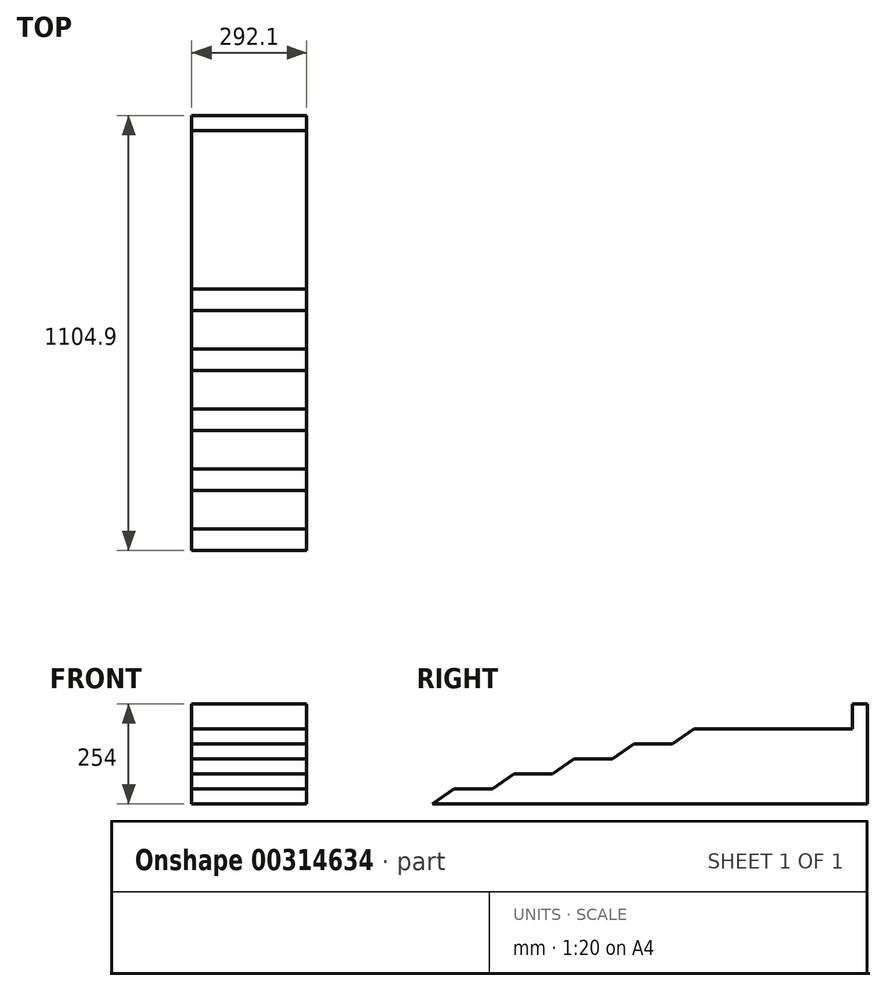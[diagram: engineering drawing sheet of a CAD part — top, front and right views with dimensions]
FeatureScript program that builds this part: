
annotation { "Feature Type Name" : "Feature", "Feature Type Description" : "" }
export const myFeature = defineFeature(function(context is Context, id is Id, definition is map)
    precondition{}
    {
        {
            var Q0;
            Q0=qCreatedBy(makeId("Right.planeOp"),FACE);
            var sketch = newSketch(context, id + "F0", { "sketchPlane" : qUnion([Q0])});
            skLineSegment(sketch, "E0.bottom", {"start": v(0, 0) * mm, "end": v(1066.8, 0) * mm});
            skLineSegment(sketch, "E0.top", {"start": v(0, 38.1) * mm, "end": v(1066.8, 38.1) * mm});
            skLineSegment(sketch, "E0.left", {"start": v(0, 0) * mm, "end": v(0, 38.1) * mm});
            skLineSegment(sketch, "E0.right", {"start": v(1066.8, 0) * mm, "end": v(1066.8, 38.1) * mm});
            skSolve(sketch);
        }
        {
            var Q0;
            Q0 = qSketchRegion(id + "F0", true);
            extrude(context, id + "F1", {"entities" : qUnion([Q0]), "depth" : 292.1 * mm});
        }
        {
            var Q0;
            Q0=qCreatedBy(makeId("Right.planeOp"),FACE);
            var sketch = newSketch(context, id + "F2", { "sketchPlane" : qUnion([Q0])});
            skLineSegment(sketch, "E1.bottom", {"start": v(1066.8, 38.1) * mm, "end": v(152.4, 38.1) * mm});
            skLineSegment(sketch, "E1.top", {"start": v(1066.8, 76.2) * mm, "end": v(152.4, 76.2) * mm});
            skLineSegment(sketch, "E1.left", {"start": v(1066.8, 38.1) * mm, "end": v(1066.8, 76.2) * mm});
            skLineSegment(sketch, "E1.right", {"start": v(152.4, 38.1) * mm, "end": v(152.4, 76.2) * mm});
            skSolve(sketch);
        }
        {
            var Q0;
            Q0 = qSketchRegion(id + "F2", true);
            var Q1;
            Q1=makeQuery(id+"F1.opExtrude","CAP_FACE",FACE,{"disambiguationData":[OSD([sQuery(id+"F0.wireOp",EDGE,"E0.bottom"),sQuery(id+"F0.wireOp",EDGE,"E0.top"),sQuery(id+"F0.wireOp",EDGE,"E0.left"),sQuery(id+"F0.wireOp",EDGE,"E0.right")])],"isStart":false});
            extrude(context, id + "F3", {"entities" : qUnion([Q0]), "operationType" : NewBodyOperationType.ADD, "endBound" : BoundingType.UP_TO_SURFACE, "endBoundEntityFace" : qUnion([Q1]), "depth" : 25.4 * mm});
        }
        {
            var Q0;
            Q0=qCreatedBy(makeId("Right.planeOp"),FACE);
            var sketch = newSketch(context, id + "F4", { "sketchPlane" : qUnion([Q0])});
            skLineSegment(sketch, "E2.bottom", {"start": v(1066.8, 76.2) * mm, "end": v(304.8, 76.2) * mm});
            skLineSegment(sketch, "E2.top", {"start": v(1066.8, 114.3) * mm, "end": v(304.8, 114.3) * mm});
            skLineSegment(sketch, "E2.left", {"start": v(1066.8, 76.2) * mm, "end": v(1066.8, 114.3) * mm});
            skLineSegment(sketch, "E2.right", {"start": v(304.8, 76.2) * mm, "end": v(304.8, 114.3) * mm});
            skSolve(sketch);
        }
        {
            var Q0;
            Q0 = qSketchRegion(id + "F4", true);
            var Q1;
            {var subQ0=sQuery(id+"F0.wireOp",EDGE,"E0.right");var subQ1=sQuery(id+"F0.wireOp",EDGE,"E0.left");var subQ2=sQuery(id+"F0.wireOp",EDGE,"E0.top");var subQ3=sQuery(id+"F0.wireOp",EDGE,"E0.bottom");Q1=makeQuery(id+"F3.boolean.opBoolean","MERGE",FACE,{"derivedFrom":[makeQuery(id+"F1.opExtrude","CAP_FACE",FACE,{"disambiguationData":[OSD([subQ3,subQ2,subQ1,subQ0])],"isStart":false}),makeQuery(id+"F3.opExtrude","CAP_FACE",FACE,{"disambiguationData":[OSD([subQ3,subQ2,subQ1,subQ0])],"isStart":false})]});}
            extrude(context, id + "F5", {"entities" : qUnion([Q0]), "operationType" : NewBodyOperationType.ADD, "endBound" : BoundingType.UP_TO_SURFACE, "endBoundEntityFace" : qUnion([Q1]), "depth" : 25.4 * mm});
        }
        {
            var Q0;
            Q0=qCreatedBy(makeId("Right.planeOp"),FACE);
            var sketch = newSketch(context, id + "F6", { "sketchPlane" : qUnion([Q0])});
            skLineSegment(sketch, "E3.bottom", {"start": v(457.2, 152.4) * mm, "end": v(1066.8, 152.4) * mm});
            skLineSegment(sketch, "E3.top", {"start": v(457.2, 114.3) * mm, "end": v(1066.8, 114.3) * mm});
            skLineSegment(sketch, "E3.left", {"start": v(457.2, 152.4) * mm, "end": v(457.2, 114.3) * mm});
            skLineSegment(sketch, "E3.right", {"start": v(1066.8, 152.4) * mm, "end": v(1066.8, 114.3) * mm});
            skSolve(sketch);
        }
        {
            var Q0;
            Q0 = qSketchRegion(id + "F6", true);
            var Q1;
            {var subQ0=sQuery(id+"F0.wireOp",EDGE,"E0.right");var subQ1=sQuery(id+"F0.wireOp",EDGE,"E0.left");var subQ2=sQuery(id+"F0.wireOp",EDGE,"E0.top");var subQ3=sQuery(id+"F0.wireOp",EDGE,"E0.bottom");Q1=makeQuery(id+"F5.boolean.opBoolean","MERGE",FACE,{"derivedFrom":[makeQuery(id+"F3.boolean.opBoolean","MERGE",FACE,{"derivedFrom":[makeQuery(id+"F1.opExtrude","CAP_FACE",FACE,{"disambiguationData":[OSD([subQ3,subQ2,subQ1,subQ0])],"isStart":false}),makeQuery(id+"F3.opExtrude","CAP_FACE",FACE,{"disambiguationData":[OSD([subQ3,subQ2,subQ1,subQ0])],"isStart":false})]}),makeQuery(id+"F5.opExtrude","CAP_FACE",FACE,{"disambiguationData":[OSD([subQ3,subQ2,subQ1,subQ0])],"isStart":false})]});}
            extrude(context, id + "F7", {"entities" : qUnion([Q0]), "operationType" : NewBodyOperationType.ADD, "endBound" : BoundingType.UP_TO_SURFACE, "endBoundEntityFace" : qUnion([Q1]), "depth" : 25.4 * mm});
        }
        {
            var Q0;
            Q0=qCreatedBy(makeId("Right.planeOp"),FACE);
            var sketch = newSketch(context, id + "F8", { "sketchPlane" : qUnion([Q0])});
            skLineSegment(sketch, "E4.bottom", {"start": v(609.6, 190.5) * mm, "end": v(1066.8, 190.5) * mm});
            skLineSegment(sketch, "E4.top", {"start": v(609.6, 152.4) * mm, "end": v(1066.8, 152.4) * mm});
            skLineSegment(sketch, "E4.left", {"start": v(609.6, 190.5) * mm, "end": v(609.6, 152.4) * mm});
            skLineSegment(sketch, "E4.right", {"start": v(1066.8, 190.5) * mm, "end": v(1066.8, 152.4) * mm});
            skSolve(sketch);
        }
        {
            var Q0;
            Q0 = qSketchRegion(id + "F8", true);
            var Q1;
            {var subQ0=sQuery(id+"F0.wireOp",EDGE,"E0.right");var subQ1=sQuery(id+"F0.wireOp",EDGE,"E0.left");var subQ2=sQuery(id+"F0.wireOp",EDGE,"E0.top");var subQ3=sQuery(id+"F0.wireOp",EDGE,"E0.bottom");Q1=makeQuery(id+"F7.boolean.opBoolean","MERGE",FACE,{"derivedFrom":[makeQuery(id+"F5.boolean.opBoolean","MERGE",FACE,{"derivedFrom":[makeQuery(id+"F3.boolean.opBoolean","MERGE",FACE,{"derivedFrom":[makeQuery(id+"F1.opExtrude","CAP_FACE",FACE,{"disambiguationData":[OSD([subQ3,subQ2,subQ1,subQ0])],"isStart":false}),makeQuery(id+"F3.opExtrude","CAP_FACE",FACE,{"disambiguationData":[OSD([subQ3,subQ2,subQ1,subQ0])],"isStart":false})]}),makeQuery(id+"F5.opExtrude","CAP_FACE",FACE,{"disambiguationData":[OSD([subQ3,subQ2,subQ1,subQ0])],"isStart":false})]}),makeQuery(id+"F7.opExtrude","CAP_FACE",FACE,{"disambiguationData":[OSD([subQ3,subQ2,subQ1,subQ0])],"isStart":false})]});}
            extrude(context, id + "F9", {"entities" : qUnion([Q0]), "operationType" : NewBodyOperationType.ADD, "endBound" : BoundingType.UP_TO_SURFACE, "endBoundEntityFace" : qUnion([Q1]), "depth" : 25.4 * mm});
        }
        {
            var Q0;
            Q0=makeQuery(id+"F1.opExtrude","SWEPT_EDGE",EDGE,{"disambiguationData":[OSD([sQuery(id+"F0.wireOp",EDGE,"E0.top"),sQuery(id+"F0.wireOp",EDGE,"E0.left")])]});
            var Q1;
            Q1=makeQuery(id+"F3.opExtrude","SWEPT_EDGE",EDGE,{"disambiguationData":[OSD([sQuery(id+"F2.wireOp",EDGE,"E1.top"),sQuery(id+"F2.wireOp",EDGE,"E1.right")])]});
            var Q2;
            Q2=makeQuery(id+"F5.opExtrude","SWEPT_EDGE",EDGE,{"disambiguationData":[OSD([sQuery(id+"F4.wireOp",EDGE,"E2.top"),sQuery(id+"F4.wireOp",EDGE,"E2.right")])]});
            var Q3;
            Q3=makeQuery(id+"F7.opExtrude","SWEPT_EDGE",EDGE,{"disambiguationData":[OSD([sQuery(id+"F6.wireOp",EDGE,"E3.bottom"),sQuery(id+"F6.wireOp",EDGE,"E3.left")])]});
            var Q4;
            Q4=makeQuery(id+"F9.opExtrude","SWEPT_EDGE",EDGE,{"disambiguationData":[OSD([sQuery(id+"F8.wireOp",EDGE,"E4.bottom"),sQuery(id+"F8.wireOp",EDGE,"E4.left")])]});
            chamfer(context, id + "F10", {"entities" : qUnion([Q0, Q1, Q2, Q3, Q4]), "chamferType" : ChamferType.OFFSET_ANGLE, "width" : 38.1 * mm, "oppositeDirection" : false, "angle" : 55 * degree, "tangentPropagation" : true});
        }
        {
            var Q0;
            Q0=qCreatedBy(makeId("Top.planeOp"),FACE);
            var sketch = newSketch(context, id + "F11", { "sketchPlane" : qUnion([Q0])});
            skLineSegment(sketch, "E5.bottom", {"start": v(0, 1066.8) * mm, "end": v(292.1, 1066.8) * mm});
            skLineSegment(sketch, "E5.top", {"start": v(0, 1104.9) * mm, "end": v(292.1, 1104.9) * mm});
            skLineSegment(sketch, "E5.left", {"start": v(0, 1066.8) * mm, "end": v(0, 1104.9) * mm});
            skLineSegment(sketch, "E5.right", {"start": v(292.1, 1066.8) * mm, "end": v(292.1, 1104.9) * mm});
            skSolve(sketch);
        }
        {
            var Q0;
            Q0 = qSketchRegion(id + "F11", true);
            extrude(context, id + "F12", {"entities" : qUnion([Q0]), "operationType" : NewBodyOperationType.ADD, "depth" : 254 * mm});
        }
    });
